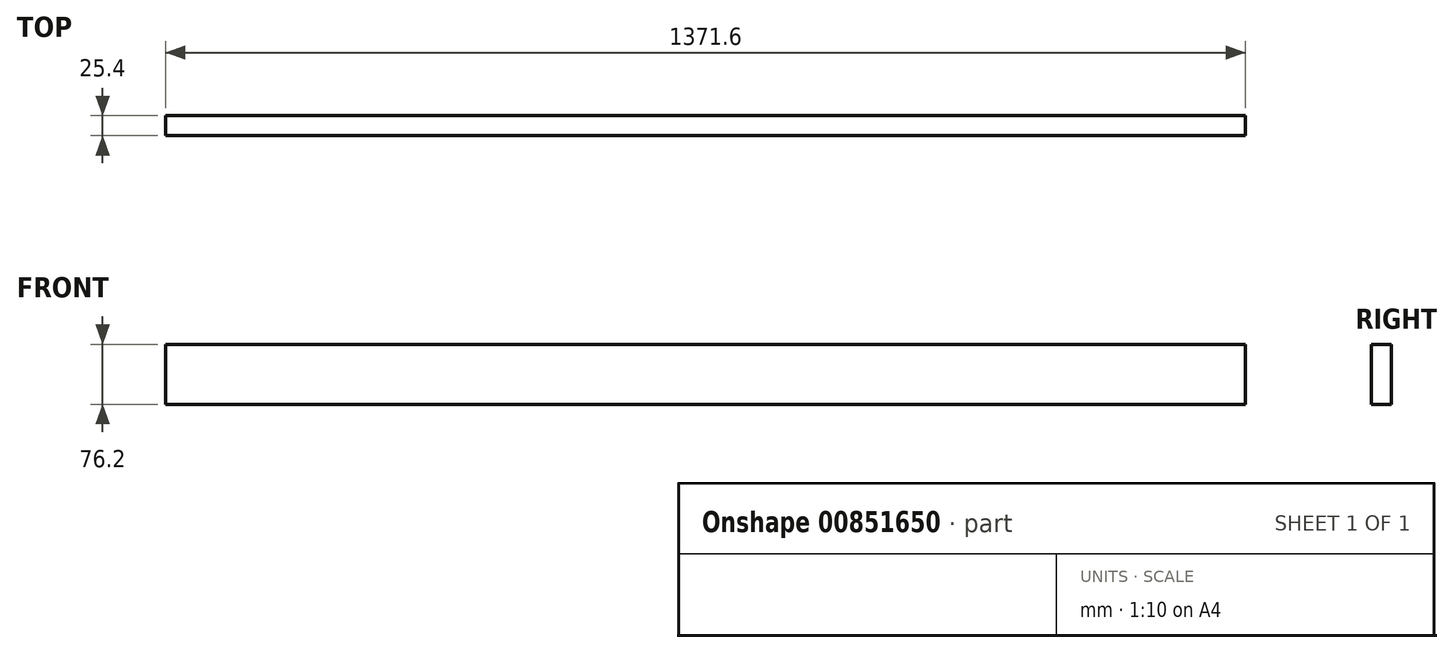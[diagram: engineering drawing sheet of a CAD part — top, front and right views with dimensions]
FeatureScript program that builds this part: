
annotation { "Feature Type Name" : "Feature", "Feature Type Description" : "" }
export const myFeature = defineFeature(function(context is Context, id is Id, definition is map)
    precondition{}
    {
        {
            var Q0;
            Q0=qCreatedBy(makeId("Top.planeOp"),FACE);
            var sketch = newSketch(context, id + "F0", { "sketchPlane" : qUnion([Q0])});
            skLineSegment(sketch, "E0", {"start": v(-688.98, -16.78) * mm, "end": v(682.62, -16.78) * mm});
            skLineSegment(sketch, "E1", {"start": v(-688.98, -16.78) * mm, "end": v(-688.98, -42.18) * mm});
            skLineSegment(sketch, "E2", {"start": v(-688.98, -42.18) * mm, "end": v(682.62, -42.18) * mm});
            skLineSegment(sketch, "E3", {"start": v(682.62, -42.18) * mm, "end": v(682.62, -16.78) * mm});
            skSolve(sketch);
        }
        {
            var Q0;
            Q0 = qSketchRegion(id + "F0", true);
            extrude(context, id + "F1", {"entities" : qUnion([Q0]), "depth" : 76.2 * mm, "offsetDistance" : 25.4 * mm});
        }
    });
